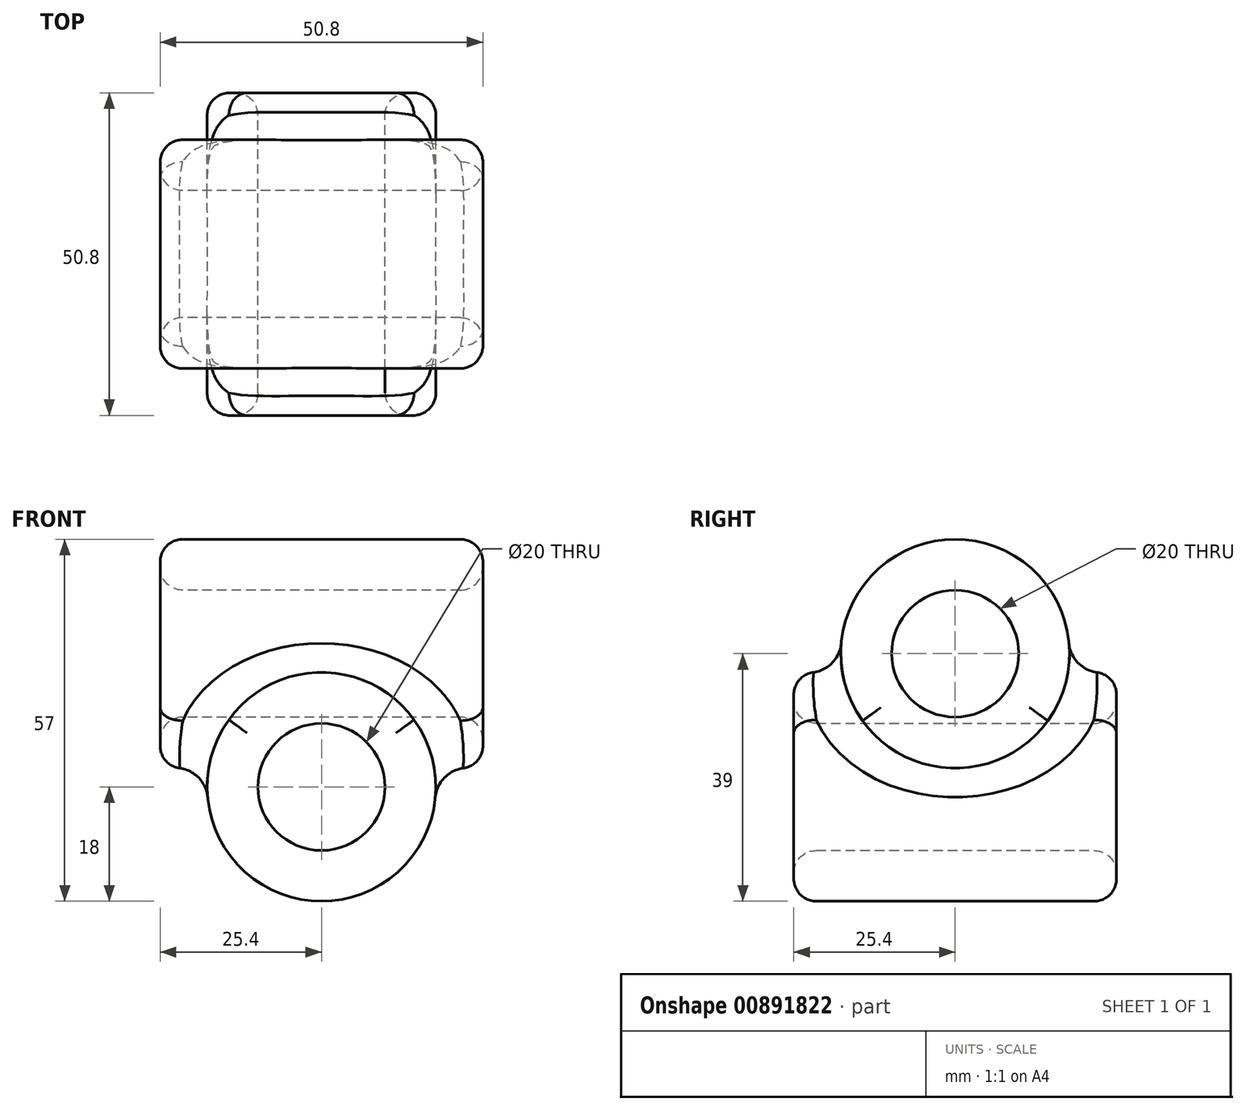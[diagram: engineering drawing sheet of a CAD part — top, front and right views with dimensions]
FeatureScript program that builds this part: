
annotation { "Feature Type Name" : "Feature", "Feature Type Description" : "" }
export const myFeature = defineFeature(function(context is Context, id is Id, definition is map)
    precondition{}
    {
        {
            var Q0;
            Q0=qCreatedBy(makeId("Front.planeOp"),FACE);
            var sketch = newSketch(context, id + "F0", { "sketchPlane" : qUnion([Q0])});
            skCircle(sketch, "E0", {"center": v(0, 0) * mm, "radius": 10 * mm});
            skCircle(sketch, "E1", {"center": v(0, 0) * mm, "radius": 18 * mm});
            skSolve(sketch);
        }
        {
            var Q0;
            Q0=makeQuery(id+"F0.imprint","IMPRINT",FACE,{"disambiguationData":[TD([[makeQuery(id+"F0.imprint","IMPRINT",EDGE,{"derivedFrom":sQuery(id+"F0.wireOp",EDGE,"E0")}),-1.0]])]});
            extrude(context, id + "F1", {"entities" : qUnion([Q0]), "endBound" : BoundingType.SYMMETRIC, "depth" : 50.8 * mm, "offsetDistance" : 25.4 * mm});
        }
        {
            var Q0;
            Q0=qCreatedBy(makeId("Right.planeOp"),FACE);
            var sketch = newSketch(context, id + "F2", { "sketchPlane" : qUnion([Q0])});
            skCircle(sketch, "E2", {"center": v(0, 21) * mm, "radius": 10 * mm});
            skCircle(sketch, "E3", {"center": v(0, 21) * mm, "radius": 18 * mm});
            skSolve(sketch);
        }
        {
            var Q0;
            Q0=makeQuery(id+"F2.imprint","IMPRINT",FACE,{"disambiguationData":[TD([[makeQuery(id+"F2.imprint","IMPRINT",EDGE,{"derivedFrom":sQuery(id+"F2.wireOp",EDGE,"E2")}),-1.0]])]});
            extrude(context, id + "F3", {"entities" : qUnion([Q0]), "operationType" : NewBodyOperationType.ADD, "endBound" : BoundingType.SYMMETRIC, "depth" : 50.8 * mm, "offsetDistance" : 25.4 * mm});
        }
        {
            var Q0;
            Q0=makeQuery(id+"F0.imprint","IMPRINT",FACE,{"disambiguationData":[TD([[makeQuery(id+"F0.imprint","IMPRINT",EDGE,{"derivedFrom":sQuery(id+"F0.wireOp",EDGE,"E0")}),1.0]])]});
            extrude(context, id + "F4", {"entities" : qUnion([Q0]), "operationType" : NewBodyOperationType.REMOVE, "endBound" : BoundingType.SYMMETRIC, "depth" : 76.2 * mm, "offsetDistance" : 25.4 * mm});
        }
        {
            var Q0;
            Q0=makeQuery(id+"F2.imprint","IMPRINT",FACE,{"disambiguationData":[TD([[makeQuery(id+"F2.imprint","IMPRINT",EDGE,{"derivedFrom":sQuery(id+"F2.wireOp",EDGE,"E2")}),1.0]])]});
            extrude(context, id + "F5", {"entities" : qUnion([Q0]), "operationType" : NewBodyOperationType.REMOVE, "endBound" : BoundingType.SYMMETRIC, "oppositeDirection" : true, "depth" : 76.2 * mm, "offsetDistance" : 25.4 * mm});
        }
        {
            var Q0;
            Q0=makeQuery(id+"F3.boolean.opBoolean","INTERSECT",EDGE,{"derivedFrom":[makeQuery(id+"F1.opExtrude","SWEPT_FACE",FACE,{"disambiguationData":[OSD([sQuery(id+"F0.wireOp",EDGE,"E1")])]}),makeQuery(id+"F3.opExtrude","SWEPT_FACE",FACE,{"disambiguationData":[OSD([sQuery(id+"F2.wireOp",EDGE,"E3")])]})]});
            fillet(context, id + "F6", {"entities" : qUnion([Q0]), "radius" : 5.08 * mm, "tangentPropagation" : true, "allowEdgeOverflow" : false});
        }
        {
            var Q0;
            Q0=makeQuery(id+"F3.opExtrude","CAP_EDGE",EDGE,{"disambiguationData":[OSD([sQuery(id+"F2.wireOp",EDGE,"E3")])],"isStart":false});
            var Q1;
            Q1=makeQuery(id+"F3.opExtrude","CAP_EDGE",EDGE,{"disambiguationData":[OSD([sQuery(id+"F2.wireOp",EDGE,"E2")])],"isStart":false});
            var Q2;
            Q2=makeQuery(id+"F1.opExtrude","CAP_EDGE",EDGE,{"disambiguationData":[OSD([sQuery(id+"F0.wireOp",EDGE,"E1")])],"isStart":false});
            var Q3;
            Q3=makeQuery(id+"F1.opExtrude","CAP_EDGE",EDGE,{"disambiguationData":[OSD([sQuery(id+"F0.wireOp",EDGE,"E0")])],"isStart":false});
            var Q4;
            Q4=makeQuery(id+"F1.opExtrude","CAP_EDGE",EDGE,{"disambiguationData":[OSD([sQuery(id+"F0.wireOp",EDGE,"E1")])],"isStart":true});
            var Q5;
            Q5=makeQuery(id+"F1.opExtrude","CAP_EDGE",EDGE,{"disambiguationData":[OSD([sQuery(id+"F0.wireOp",EDGE,"E0")])],"isStart":true});
            var Q6;
            Q6=makeQuery(id+"F3.opExtrude","CAP_EDGE",EDGE,{"disambiguationData":[OSD([sQuery(id+"F2.wireOp",EDGE,"E3")])],"isStart":true});
            var Q7;
            Q7=makeQuery(id+"F3.opExtrude","CAP_EDGE",EDGE,{"disambiguationData":[OSD([sQuery(id+"F2.wireOp",EDGE,"E2")])],"isStart":true});
            fillet(context, id + "F7", {"entities" : qUnion([Q0, Q1, Q2, Q3, Q4, Q5, Q6, Q7]), "radius" : 3.56 * mm, "tangentPropagation" : true, "allowEdgeOverflow" : false});
        }
    });
